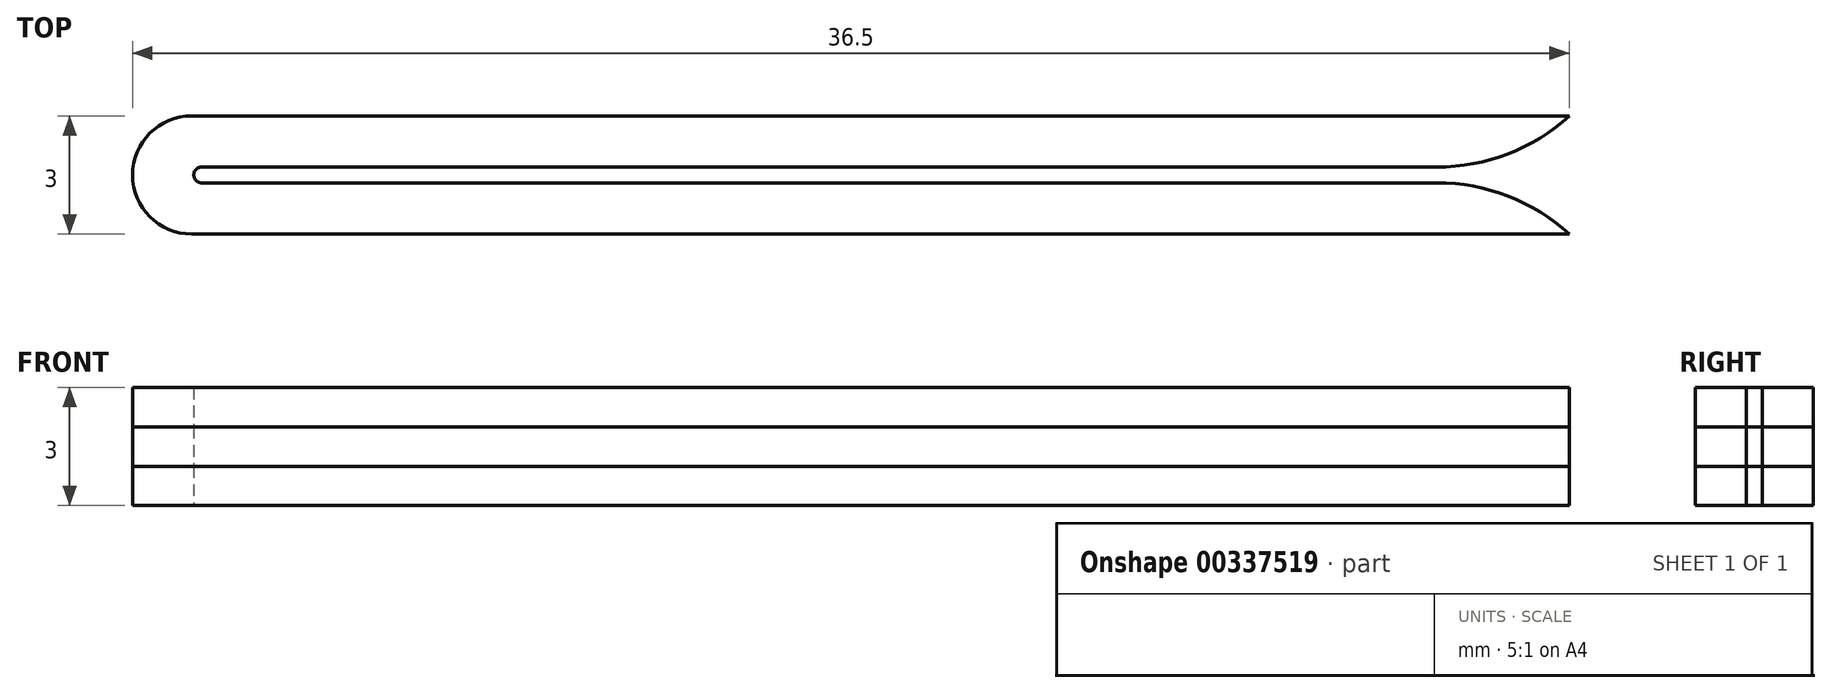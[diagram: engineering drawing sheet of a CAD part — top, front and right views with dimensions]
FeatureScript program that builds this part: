
annotation { "Feature Type Name" : "Feature", "Feature Type Description" : "" }
export const myFeature = defineFeature(function(context is Context, id is Id, definition is map)
    precondition{}
    {
        {
            var Q0;
            Q0=qCreatedBy(makeId("Top.planeOp"),FACE);
            var sketch = newSketch(context, id + "F0", { "sketchPlane" : qUnion([Q0])});
            skArc(sketch, "E0", {"start": v(0, 1.5) * mm, "mid": v(-1.5, 0) * mm, "end": v(0, -1.5) * mm});
            skLineSegment(sketch, "E1", {"start": v(0, -1.5) * mm, "end": v(35, -1.5) * mm});
            skLineSegment(sketch, "E2.0", {"start": v(0.25, -0.2) * mm, "end": v(35, -0.2) * mm});
            skLineSegment(sketch, "E3", {"start": v(0, 1.5) * mm, "end": v(35, 1.5) * mm});
            skLineSegment(sketch, "E4.0", {"start": v(0.25, 0.2) * mm, "end": v(35, 0.2) * mm});
            skArc(sketch, "E5", {"start": v(0.25, 0.2) * mm, "mid": v(0.05, 0) * mm, "end": v(0.25, -0.2) * mm});
            skLineSegment(sketch, "E6", {"start": v(35, 1.5) * mm, "end": v(35, 0.2) * mm});
            skLineSegment(sketch, "E7", {"start": v(35, -0.2) * mm, "end": v(35, -1.5) * mm});
            skSolve(sketch);
        }
        {
            var Q0;
            Q0=makeQuery(id+"F0.imprint","IMPRINT",FACE,{"disambiguationData":[TD([[makeQuery(id+"F0.imprint","IMPRINT",EDGE,{"derivedFrom":sQuery(id+"F0.wireOp",EDGE,"E0")}),1.0]])]});
            extrude(context, id + "F1", {"entities" : qUnion([Q0]), "depth" : 1 * mm});
        }
        {
            var Q0;
            Q0=makeQuery(id+"F1.opExtrude","CAP_FACE",FACE,{"disambiguationData":[OSD([sQuery(id+"F0.wireOp",EDGE,"E0"),sQuery(id+"F0.wireOp",EDGE,"E1"),sQuery(id+"F0.wireOp",EDGE,"E2.0"),sQuery(id+"F0.wireOp",EDGE,"E3"),sQuery(id+"F0.wireOp",EDGE,"E4.0"),sQuery(id+"F0.wireOp",EDGE,"E5"),sQuery(id+"F0.wireOp",EDGE,"E6"),sQuery(id+"F0.wireOp",EDGE,"E7")])],"isStart":false});
            extrude(context, id + "F2", {"entities" : qUnion([Q0]), "depth" : 1 * mm});
        }
        {
            var Q0;
            Q0=makeQuery(id+"F2.opExtrude","CAP_FACE",FACE,{"disambiguationData":[OSD([sQuery(id+"F0.wireOp",EDGE,"E0"),sQuery(id+"F0.wireOp",EDGE,"E1"),sQuery(id+"F0.wireOp",EDGE,"E2.0"),sQuery(id+"F0.wireOp",EDGE,"E3"),sQuery(id+"F0.wireOp",EDGE,"E4.0"),sQuery(id+"F0.wireOp",EDGE,"E5"),sQuery(id+"F0.wireOp",EDGE,"E6"),sQuery(id+"F0.wireOp",EDGE,"E7")])],"isStart":false});
            extrude(context, id + "F3", {"entities" : qUnion([Q0]), "depth" : 1 * mm});
        }
        {
            var Q0;
            Q0=makeQuery(id+"F2.opExtrude","SWEPT_EDGE",EDGE,{"disambiguationData":[OSD([sQuery(id+"F0.wireOp",EDGE,"E4.0"),sQuery(id+"F0.wireOp",EDGE,"E6")])]});
            var Q1;
            Q1=makeQuery(id+"F1.opExtrude","SWEPT_EDGE",EDGE,{"disambiguationData":[OSD([sQuery(id+"F0.wireOp",EDGE,"E4.0"),sQuery(id+"F0.wireOp",EDGE,"E6")])]});
            var Q2;
            Q2=makeQuery(id+"F1.opExtrude","SWEPT_EDGE",EDGE,{"disambiguationData":[OSD([sQuery(id+"F0.wireOp",EDGE,"E2.0"),sQuery(id+"F0.wireOp",EDGE,"E7")])]});
            var Q3;
            Q3=makeQuery(id+"F2.opExtrude","SWEPT_EDGE",EDGE,{"disambiguationData":[OSD([sQuery(id+"F0.wireOp",EDGE,"E2.0"),sQuery(id+"F0.wireOp",EDGE,"E7")])]});
            var Q4;
            Q4=makeQuery(id+"F3.opExtrude","SWEPT_EDGE",EDGE,{"disambiguationData":[OSD([sQuery(id+"F0.wireOp",EDGE,"E2.0"),sQuery(id+"F0.wireOp",EDGE,"E7")])]});
            var Q5;
            Q5=makeQuery(id+"F3.opExtrude","SWEPT_EDGE",EDGE,{"disambiguationData":[OSD([sQuery(id+"F0.wireOp",EDGE,"E4.0"),sQuery(id+"F0.wireOp",EDGE,"E6")])]});
            fillet(context, id + "F4", {"entities" : qUnion([Q0, Q1, Q2, Q3, Q4, Q5]), "radius" : 5 * mm, "tangentPropagation" : true, "allowEdgeOverflow" : false});
        }
    });
